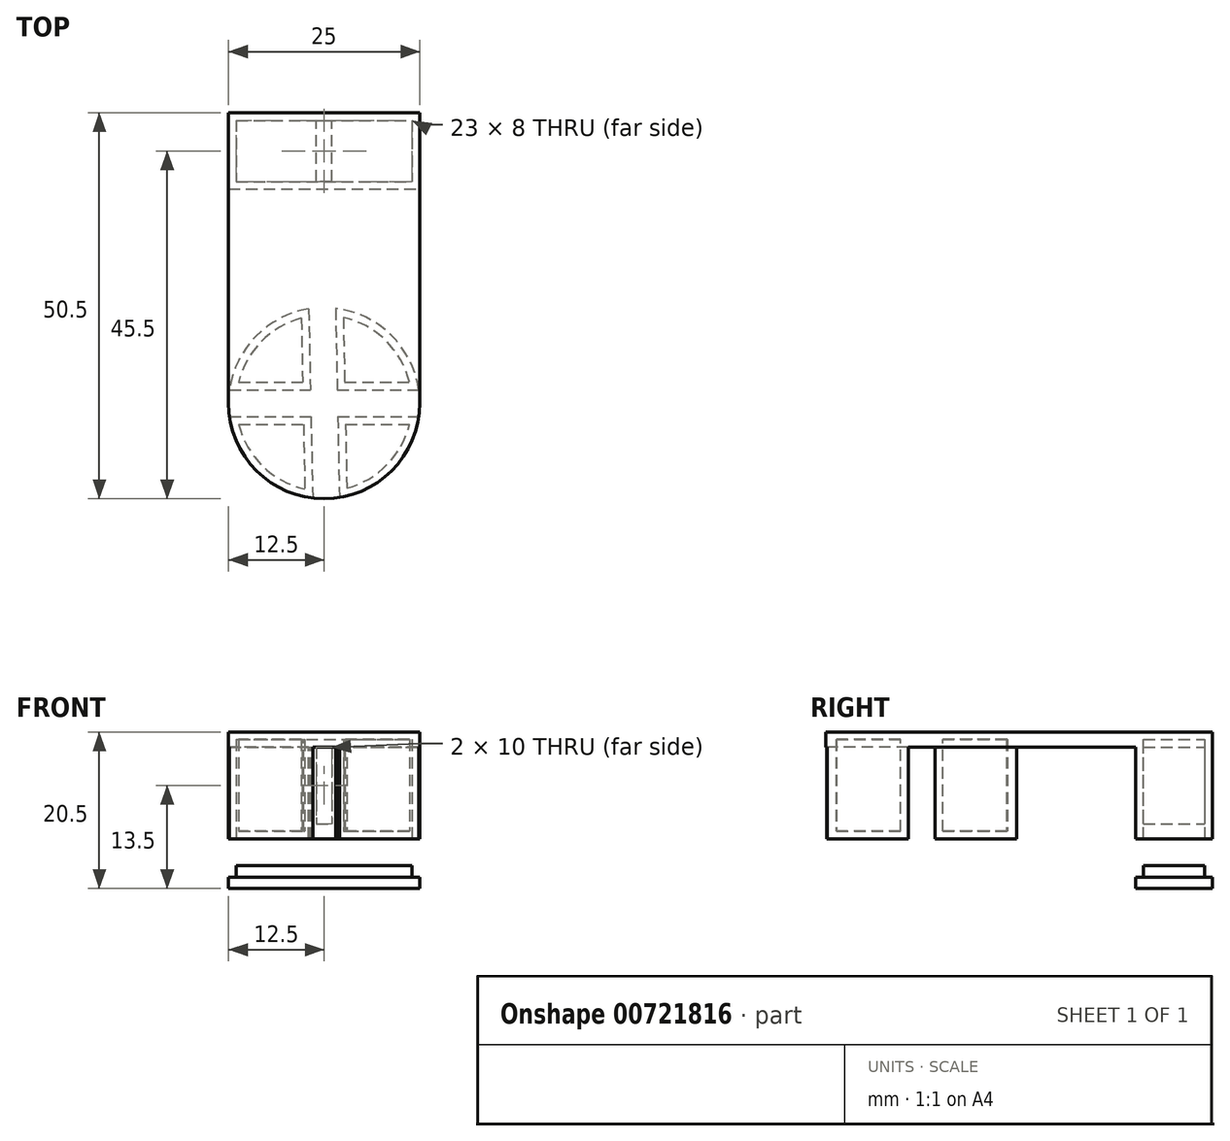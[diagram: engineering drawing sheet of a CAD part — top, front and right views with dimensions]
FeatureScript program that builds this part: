
annotation { "Feature Type Name" : "Feature", "Feature Type Description" : "" }
export const myFeature = defineFeature(function(context is Context, id is Id, definition is map)
    precondition{}
    {
        {
            var Q0;
            Q0=qCreatedBy(makeId("Top.planeOp"),FACE);
            var sketch = newSketch(context, id + "F0", { "sketchPlane" : qUnion([Q0])});
            skArc(sketch, "E0", {"start": v(-12.38, -1.75) * mm, "mid": v(-8.75, -8.93) * mm, "end": v(-1.5, -12.41) * mm});
            skLineSegment(sketch, "E1.left", {"start": v(-2, 12.34) * mm, "end": v(-1.79, 1.75) * mm});
            skLineSegment(sketch, "E1.right", {"start": v(1.5, 12.41) * mm, "end": v(1.71, 1.75) * mm});
            skLineSegment(sketch, "E2.bottom", {"start": v(-12.38, 1.75) * mm, "end": v(-1.79, 1.75) * mm});
            skLineSegment(sketch, "E2.top", {"start": v(-12.38, -1.75) * mm, "end": v(-1.71, -1.75) * mm});
            skPoint(sketch, "E2.left.start.orphan", {"position": v(-12.07, 1.75) * mm});
            skPoint(sketch, "E3.orphan", {"position": v(-25.04, -1.75) * mm});
            skArc(sketch, "E4.trimOffspring", {"start": v(2, -12.34) * mm, "mid": v(8.93, -8.75) * mm, "end": v(12.38, -1.75) * mm});
            skPoint(sketch, "E1.top.start.orphan", {"position": v(-1.42, -16.08) * mm});
            skPoint(sketch, "E5.orphan", {"position": v(2.08, -16.14) * mm});
            skPoint(sketch, "E2.right.end.orphan", {"position": v(12.07, -1.75) * mm});
            skPoint(sketch, "E2.right.start.orphan", {"position": v(25.04, 1.75) * mm});
            skArc(sketch, "E6.trimOffspring", {"start": v(12.38, 1.75) * mm, "mid": v(8.75, 8.93) * mm, "end": v(1.5, 12.41) * mm});
            skArc(sketch, "E7.trimOffspring", {"start": v(-2, 12.34) * mm, "mid": v(-8.93, 8.75) * mm, "end": v(-12.38, 1.75) * mm});
            skPoint(sketch, "E8.orphan", {"position": v(-2.08, 16.14) * mm});
            skPoint(sketch, "E9.orphan", {"position": v(1.42, 16.08) * mm});
            skLineSegment(sketch, "E10.trimOffspring", {"start": v(1.71, 1.75) * mm, "end": v(12.38, 1.75) * mm});
            skLineSegment(sketch, "E11.trimOffspring", {"start": v(1.79, -1.75) * mm, "end": v(12.38, -1.75) * mm});
            skLineSegment(sketch, "E12.trimOffspring", {"start": v(1.79, -1.75) * mm, "end": v(2, -12.34) * mm});
            skLineSegment(sketch, "E13.trimOffspring", {"start": v(-1.71, -1.75) * mm, "end": v(-1.5, -12.41) * mm});
            skSolve(sketch);
        }
        {
            var Q0;
            Q0=qCreatedBy(makeId("Top.planeOp"),FACE);
            var sketch = newSketch(context, id + "F1", { "sketchPlane" : qUnion([Q0])});
            skArc(sketch, "E14.0", {"start": v(12.38, 1.75) * mm, "mid": v(8.75, 8.93) * mm, "end": v(1.5, 12.41) * mm});
            skCircle(sketch, "E15", {"center": v(0, 0) * mm, "radius": 12.5 * mm});
            skSolve(sketch);
        }
        {
            var Q0;
            Q0 = qSketchRegion(id + "F1", true);
            extrude(context, id + "F2", {"entities" : qUnion([Q0]), "depth" : 2 * mm, "offsetDistance" : 25 * mm});
        }
        {
            var Q0;
            Q0 = qSketchRegion(id + "F0", true);
            extrude(context, id + "F3", {"entities" : qUnion([Q0]), "operationType" : NewBodyOperationType.ADD, "oppositeDirection" : true, "depth" : 12 * mm, "offsetDistance" : 25 * mm});
        }
        {
            var Q0;
            Q0=qCreatedBy(makeId("Top.planeOp"),FACE);
            var sketch = newSketch(context, id + "F4", { "sketchPlane" : qUnion([Q0])});
            skPoint(sketch, "E16.0", {"position": v(-12.5, 0) * mm});
            skPoint(sketch, "E17.0", {"position": v(12.5, 0) * mm});
            skLineSegment(sketch, "E18.bottom", {"start": v(-12.5, 0) * mm, "end": v(12.5, 0) * mm});
            skLineSegment(sketch, "E18.top", {"start": v(-12.5, 38) * mm, "end": v(12.5, 38) * mm});
            skLineSegment(sketch, "E18.left", {"start": v(-12.5, 0) * mm, "end": v(-12.5, 38) * mm});
            skLineSegment(sketch, "E18.right", {"start": v(12.5, 0) * mm, "end": v(12.5, 38) * mm});
            skSolve(sketch);
        }
        {
            var Q0;
            Q0 = qSketchRegion(id + "F4", true);
            extrude(context, id + "F5", {"entities" : qUnion([Q0]), "operationType" : NewBodyOperationType.ADD, "depth" : 2 * mm, "offsetDistance" : 25 * mm});
        }
        {
            var Q0;
            Q0=qCreatedBy(makeId("Top.planeOp"),FACE);
            var sketch = newSketch(context, id + "F6", { "sketchPlane" : qUnion([Q0])});
            skLineSegment(sketch, "E19.0", {"start": v(-12.5, 38) * mm, "end": v(12.5, 38) * mm});
            skLineSegment(sketch, "E20.top", {"start": v(-12.5, 28) * mm, "end": v(12.5, 28) * mm});
            skLineSegment(sketch, "E20.left", {"start": v(-12.5, 38) * mm, "end": v(-12.5, 28) * mm});
            skLineSegment(sketch, "E20.right", {"start": v(12.5, 38) * mm, "end": v(12.5, 28) * mm});
            skLineSegment(sketch, "E21", {"start": v(0, 38) * mm, "end": v(0, 28) * mm, "construction": true});
            skLineSegment(sketch, "E22", {"start": v(-12.5, 33) * mm, "end": v(12.5, 33) * mm, "construction": true});
            skLineSegment(sketch, "E23.bottom", {"start": v(-1, 28) * mm, "end": v(1, 28) * mm});
            skLineSegment(sketch, "E23.top", {"start": v(-1, 38) * mm, "end": v(1, 38) * mm});
            skLineSegment(sketch, "E23.left", {"start": v(-1, 28) * mm, "end": v(-1, 38) * mm});
            skLineSegment(sketch, "E23.right", {"start": v(1, 28) * mm, "end": v(1, 38) * mm});
            skPoint(sketch, "E23.middle", {"position": v(0, 33) * mm});
            skSolve(sketch);
        }
        {
            var Q0;
            {var subQ3=sQuery(id+"F6.wireOp",EDGE,"E23.left");var subQ8=makeQuery(id+"F6.imprint","IMPRINT",EDGE,{"derivedFrom":subQ3});var subQ10=sQuery(id+"F6.wireOp",EDGE,"E20.right");var subQ11=sQuery(id+"F6.wireOp",EDGE,"E20.left");Q0=qUnion([makeQuery(id+"F6.imprint","IMPRINT",FACE,{"disambiguationData":[TD([[makeQuery(id+"F6.imprint","IMPRINT",EDGE,{"derivedFrom":subQ11}),1.0]])]}),makeQuery(id+"F6.imprint","IMPRINT",FACE,{"disambiguationData":[TD([[makeQuery(id+"F6.imprint","IMPRINT",EDGE,{"derivedFrom":subQ10}),-1.0]])]}),makeQuery(id+"F6.imprint","IMPRINT",FACE,{"disambiguationData":[TD([[subQ8,-1.0]])]})]);}
            extrude(context, id + "F7", {"entities" : qUnion([Q0]), "operationType" : NewBodyOperationType.ADD, "oppositeDirection" : true, "depth" : 12 * mm, "offsetDistance" : 25 * mm});
        }
        {
            var Q0;
            Q0=makeQuery(id+"F7.opExtrude","CAP_FACE",FACE,{"disambiguationData":[OSD([sQuery(id+"F6.wireOp",EDGE,"E19.0"),sQuery(id+"F6.wireOp",EDGE,"E20.top"),sQuery(id+"F6.wireOp",EDGE,"E20.left"),sQuery(id+"F6.wireOp",EDGE,"E20.right")])],"isStart":false});
            shell(context, id + "F8", {"entities" : qUnion([Q0]), "thickness" : 1 * mm});
        }
        {
            var Q0;
            {var subQ2=sQuery(id+"F6.wireOp",EDGE,"E23.left");Q0=makeQuery(id+"F6.imprint","IMPRINT",FACE,{"disambiguationData":[TD([[makeQuery(id+"F6.imprint","IMPRINT",EDGE,{"derivedFrom":subQ2}),-1.0]])]});}
            extrude(context, id + "F9", {"entities" : qUnion([Q0]), "operationType" : NewBodyOperationType.ADD, "oppositeDirection" : true, "depth" : 10 * mm, "offsetDistance" : 25 * mm});
        }
        {
            var Q0;
            Q0=qCreatedBy(makeId("Top.planeOp"),FACE);
            var sketch = newSketch(context, id + "F10", { "sketchPlane" : qUnion([Q0])});
            skLineSegment(sketch, "E24.0", {"start": v(-12.5, 28) * mm, "end": v(12.5, 28) * mm});
            skLineSegment(sketch, "E25.0", {"start": v(-12.5, 38) * mm, "end": v(-12.5, 28) * mm});
            skLineSegment(sketch, "E26.0", {"start": v(-12.5, 38) * mm, "end": v(12.5, 38) * mm});
            skLineSegment(sketch, "E27.0", {"start": v(12.5, 38) * mm, "end": v(12.5, 28) * mm});
            skLineSegment(sketch, "E28.0", {"start": v(1, 28) * mm, "end": v(1, 38) * mm});
            skLineSegment(sketch, "E29.0", {"start": v(-1, 28) * mm, "end": v(-1, 38) * mm});
            skLineSegment(sketch, "E30.0", {"start": v(-11.5, 29) * mm, "end": v(11.5, 29) * mm});
            skLineSegment(sketch, "E31.0", {"start": v(-11.5, 37) * mm, "end": v(11.5, 37) * mm});
            skPoint(sketch, "E32.0", {"position": v(-11.5, 33) * mm});
            skLineSegment(sketch, "E33.0", {"start": v(-11.5, 37) * mm, "end": v(-11.5, 29) * mm});
            skLineSegment(sketch, "E34.0", {"start": v(11.5, 37) * mm, "end": v(11.5, 29) * mm});
            skSolve(sketch);
        }
        {
            var Q0;
            Q0=makeQuery(id+"F7.opExtrude","CAP_FACE",FACE,{"disambiguationData":[OSD([sQuery(id+"F6.wireOp",EDGE,"E19.0"),sQuery(id+"F6.wireOp",EDGE,"E20.top"),sQuery(id+"F6.wireOp",EDGE,"E20.left"),sQuery(id+"F6.wireOp",EDGE,"E20.right")])],"isStart":false});
            cPlane(context, id + "F11", {"entities" : qUnion([Q0]), "cplaneType" : CPlaneType.OFFSET, "offset" : 5 * mm, "width" : 150 * mm, "height" : 150 * mm});
        }
        {
            var Q0;
            Q0=qCreatedBy(id+"F11.planeOp",FACE);
            var sketch = newSketch(context, id + "F12", { "sketchPlane" : qUnion([Q0])});
            skLineSegment(sketch, "E35.0.0", {"start": v(-1, -37) * mm, "end": v(-11.5, -37) * mm});
            skLineSegment(sketch, "E35.0.1", {"start": v(-11.5, -37) * mm, "end": v(-11.5, -29) * mm});
            skLineSegment(sketch, "E35.0.2", {"start": v(-11.5, -29) * mm, "end": v(-1, -29) * mm});
            skLineSegment(sketch, "E36.0.0", {"start": v(11.5, -37) * mm, "end": v(1, -37) * mm});
            skLineSegment(sketch, "E36.0.2", {"start": v(1, -29) * mm, "end": v(11.5, -29) * mm});
            skLineSegment(sketch, "E36.0.3", {"start": v(11.5, -29) * mm, "end": v(11.5, -37) * mm});
            skLineSegment(sketch, "E37.0", {"start": v(12.5, -38) * mm, "end": v(12.5, -28) * mm});
            skLineSegment(sketch, "E38.0", {"start": v(-12.5, -28) * mm, "end": v(12.5, -28) * mm});
            skLineSegment(sketch, "E39.0", {"start": v(-12.5, -38) * mm, "end": v(12.5, -38) * mm});
            skLineSegment(sketch, "E40.0", {"start": v(-12.5, -38) * mm, "end": v(-12.5, -28) * mm});
            skLineSegment(sketch, "E41", {"start": v(-1, -29) * mm, "end": v(1, -29) * mm});
            skLineSegment(sketch, "E42", {"start": v(1, -37) * mm, "end": v(-1, -37) * mm});
            skSolve(sketch);
        }
        {
            var Q0;
            Q0 = qSketchRegion(id + "F12", true);
            var Q1;
            Q1=makeQuery(id+"F12.imprint","IMPRINT",FACE,{"disambiguationData":[TD([[makeQuery(id+"F12.imprint","IMPRINT",EDGE,{"derivedFrom":sQuery(id+"F12.wireOp",EDGE,"E35.0.0")}),-1.0]])]});
            extrude(context, id + "F13", {"entities" : qUnion([Q0, Q1]), "depth" : 1.5 * mm, "offsetDistance" : 25 * mm});
        }
        {
            var Q0;
            Q0=makeQuery(id+"F12.imprint","IMPRINT",FACE,{"disambiguationData":[TD([[makeQuery(id+"F12.imprint","IMPRINT",EDGE,{"derivedFrom":sQuery(id+"F12.wireOp",EDGE,"E35.0.0")}),-1.0]])]});
            extrude(context, id + "F14", {"entities" : qUnion([Q0]), "operationType" : NewBodyOperationType.ADD, "oppositeDirection" : true, "depth" : 1.5 * mm, "offsetDistance" : 25 * mm});
        }
    });
